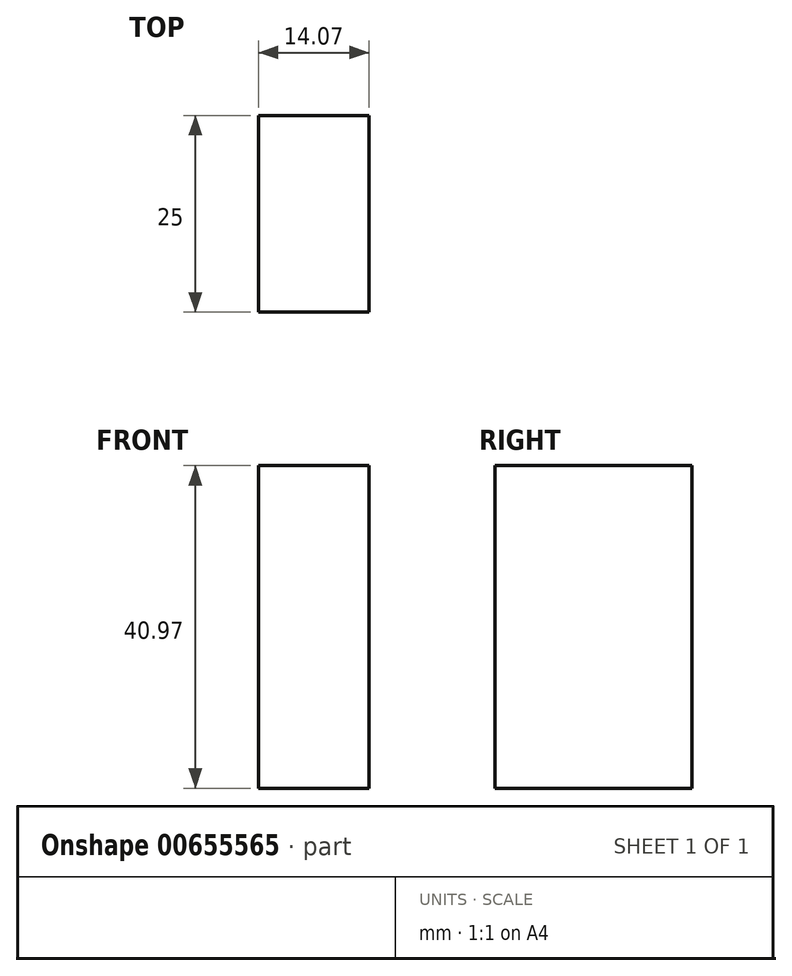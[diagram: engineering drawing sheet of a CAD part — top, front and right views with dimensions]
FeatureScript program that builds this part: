
annotation { "Feature Type Name" : "Feature", "Feature Type Description" : "" }
export const myFeature = defineFeature(function(context is Context, id is Id, definition is map)
    precondition{}
    {
        {
            var Q0;
            Q0=qCreatedBy(makeId("Front.planeOp"),FACE);
            var sketch = newSketch(context, id + "F0", { "sketchPlane" : qUnion([Q0])});
            skLineSegment(sketch, "E0", {"start": v(-47.19, 0) * mm, "end": v(-24.54, 27.47) * mm});
            skLineSegment(sketch, "E1", {"start": v(-24.54, 27.47) * mm, "end": v(23.02, 27.47) * mm});
            skLineSegment(sketch, "E2", {"start": v(23.02, 27.47) * mm, "end": v(23.02, -17.55) * mm});
            skLineSegment(sketch, "E3", {"start": v(23.02, -17.55) * mm, "end": v(37.1, -17.55) * mm});
            skLineSegment(sketch, "E4", {"start": v(37.1, -17.55) * mm, "end": v(37.1, -58.52) * mm});
            skLineSegment(sketch, "E5", {"start": v(37.1, -58.52) * mm, "end": v(23.02, -58.52) * mm});
            skLineSegment(sketch, "E6", {"start": v(23.02, -58.52) * mm, "end": v(23.02, -17.55) * mm});
            skSolve(sketch);
        }
        {
            var Q0;
            Q0 = qSketchRegion(id + "F0", true);
            var sketch = newSketch(context, id + "F1", { "sketchPlane" : qUnion([Q0])});
            skSolve(sketch);
        }
        {
            var Q0;
            Q0=makeQuery(id+"F1.imprint","IMPRINT",FACE,{"disambiguationData":[TD([[makeQuery(id+"F1.imprint","IMPRINT",EDGE,{"derivedFrom":makeQuery(id+"F0.imprint","IMPRINT",EDGE,{"derivedFrom":sQuery(id+"F0.wireOp",EDGE,"E3")})}),-1.0]])]});
            extrude(context, id + "F2", {"entities" : qUnion([Q0]), "depth" : 25 * mm, "offsetDistance" : 25 * mm});
        }
    });
